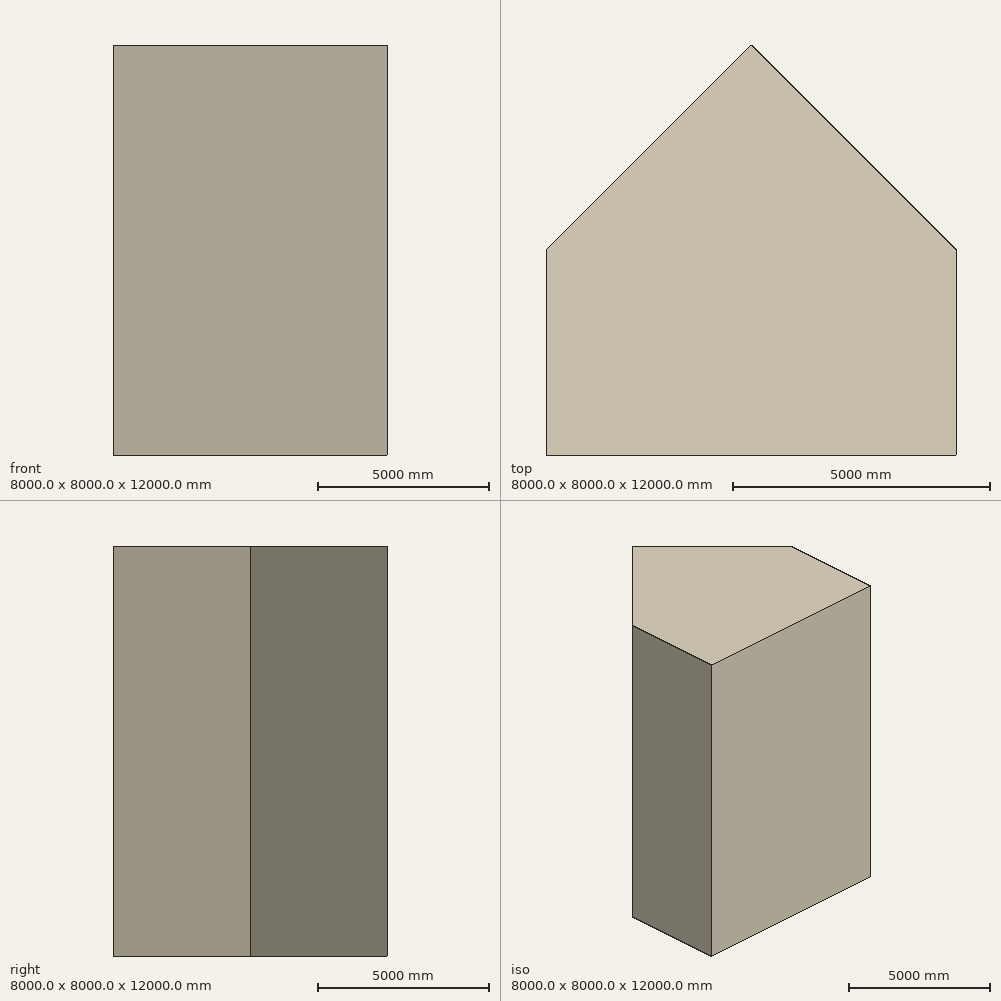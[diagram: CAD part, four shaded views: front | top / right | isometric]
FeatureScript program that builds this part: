
annotation { "Feature Type Name" : "Feature", "Feature Type Description" : "" }
export const myFeature = defineFeature(function(context is Context, id is Id, definition is map)
    precondition{}
    {
        {
            var Q0;
            Q0=qCreatedBy(makeId("Top.planeOp"),FACE);
            var sketch = newSketch(context, id + "F0", { "sketchPlane" : qUnion([Q0])});
            skLineSegment(sketch, "E0", {"start": v(0, 0) * mm, "end": v(8000, 0) * mm});
            skLineSegment(sketch, "E1", {"start": v(0, 0) * mm, "end": v(0, 4000) * mm});
            skLineSegment(sketch, "E2", {"start": v(8000, 0) * mm, "end": v(8000, 4000) * mm});
            skLineSegment(sketch, "E3", {"start": v(0, 4000) * mm, "end": v(4000, 8000) * mm});
            skLineSegment(sketch, "E4", {"start": v(4000, 8000) * mm, "end": v(8000, 4000) * mm});
            skSolve(sketch);
        }
        {
            var Q0;
            Q0=makeQuery(id+"F0.imprint","IMPRINT",FACE,{"disambiguationData":[TD([[makeQuery(id+"F0.imprint","IMPRINT",EDGE,{"derivedFrom":sQuery(id+"F0.wireOp",EDGE,"E0")}),1.0]])]});
            extrude(context, id + "F1", {"entities" : qUnion([Q0]), "depth" : 12000 * mm});
        }
    });
